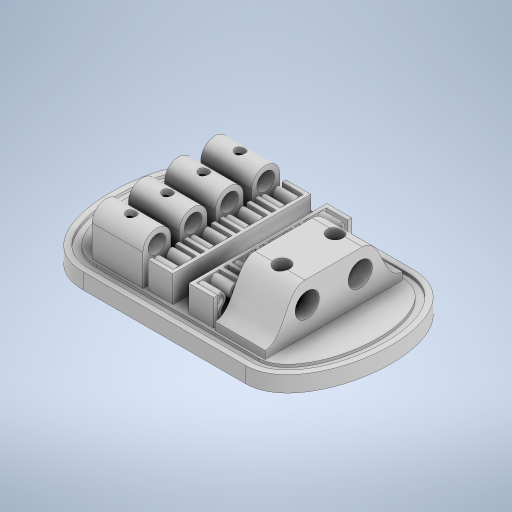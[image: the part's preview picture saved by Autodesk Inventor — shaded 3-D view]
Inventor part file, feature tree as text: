
AUTODESK INVENTOR PART (.ipt)
format: ipt  version: 2023 (Build 270158000, 158)  size: 799,232 bytes
history: native  units: in
note: dims shown in document units (in); Inventor stores cm internally (conversion verified against a paired STEP export)
features: sketch x9, extrude x8, plane x3, projected_geometry x3, mirror x1, pattern_linear x1
ambient origin geometry x8: Origin, YZ Plane, XZ Plane, XY Plane, X Axis, Y Axis, Z Axis, Center Point
bodies: Body1 (feature_tree)
feature tree (25):
  extrude  "Extrusion2"  Depth=7.874in
  sketch  "Sketch4"  dims[d33=5.9055in d34=2.9528in]
  plane  "Work Plane1"
  sketch  "Sketch5"  dims[d35=3.937in d36=1.4862in]
  extrude  "Extrusion3"  Depth=2.9528in
  extrude  "Extrusion4"  Depth=1.4862in
  extrude  "Extrusion5"  Depth=0.9843in
  plane  "Work Plane2"
  extrude  "Extrusion6"  Depth=0.9843in
  plane  "Work Plane3"
  extrude  "Extrusion7"  Depth=0.1024in
  extrude  "Extrusion8"  Depth=1.5256in
  mirror  "Mirror1"
  sketch  "Sketch10"  dims[d46=0.8701in d47=2.4409in]
  extrude  "Extrusion9"  Depth=2.4409in
  pattern_linear  "Rectangular Pattern1"  Spacing1=0.1378in  [1 undecoded]
  sketch  "Sketch3"  dims[d31=2.9724in d32=7.874in]
  projected_geometry  "Projected Loop5"
  sketch  "Sketch6"  dims[d37=2.4272in d38=0.9843in]
  projected_geometry  "Projected Loop6"
  projected_geometry  "Projected Loop7"
  sketch  "Sketch7"  dims[d39=2.9724in d40=0.9843in]
  sketch  "Sketch8"  dims[d41=0.2835in d42=0.0in d43=0.1024in]
  sketch  "Sketch9"  dims[d44=0.2264in d45=1.5256in]
  sketch  "Sketch11"  dims[d48=1.2205in d49=0.1378in d51=1.0236in d52=0.5118in d53=0.4272in d54=0.4724in d55=0.4724in d56=0.4006in d57=0.4006in d58=0.0492in d59=0.0in d60=0.8929in d61=0.0in d62=0.2756in d63=0.2756in d64=0.2756in d65=0.0in d66=1.2894in d67=0.498in d69=0.5581in d70=0.315in d71=1.5748in d73=0.6457in d74=0.3937in d76=0.3937in d78=0.9055in d79=0.0in d80=0.7992in d81=0.1732in d82=0.4508in d84=0.315in d85=0.1575in d86=1.5748in d88=0.6457in d89=0.3937in d91=0.3937in d93=0.2362in d94=0.0in d96=0.0709in d97=0.4134in d99=0.0787in d100=0.2913in d101=0.0472in d102=0.4429in d103=0.063in d104=0.3799in d105=0.4724in d106=0.0in d107=0.3543in d108=0.1181in d109=0.2362in d110=0.1181in d111=0.0591in d112=0.3543in d113=0.1772in d114=0.2362in d115=0.1181in d116=0.1772in d117=0.0886in d128=0.3543in d131=0.1181in d132=0.0787in d134=0.3543in d137=0.0197in d139=0.0197in d145=0.0197in d146=0.0197in d147=0.3543in d148=0.0in d149=1.5748in d151=0.6299in d152=0.7874in d154=0.7776in]
note: 1 required parameter value undecoded (feature->parameter linkage not recoverable at this tier; creation-order binding heuristic only, values carry confidence <= 0.55)
